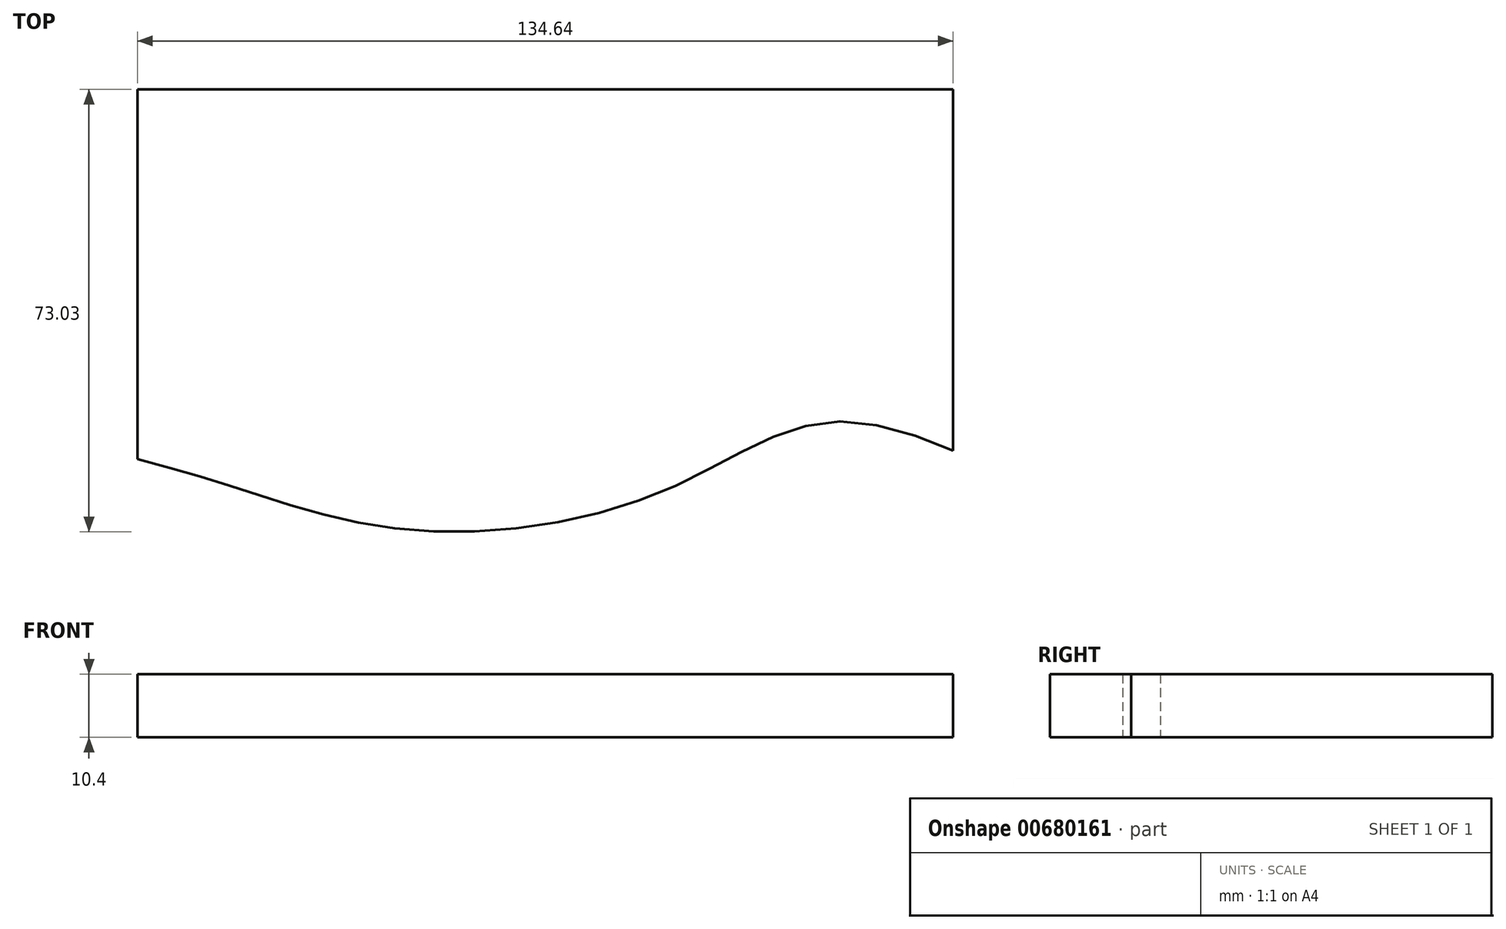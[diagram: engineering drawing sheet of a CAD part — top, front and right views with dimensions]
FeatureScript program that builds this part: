
annotation { "Feature Type Name" : "Feature", "Feature Type Description" : "" }
export const myFeature = defineFeature(function(context is Context, id is Id, definition is map)
    precondition{}
    {
        {
            var Q0;
            Q0=qCreatedBy(makeId("Top.planeOp"),FACE);
            var sketch = newSketch(context, id + "F0", { "sketchPlane" : qUnion([Q0])});
            skLineSegment(sketch, "E0.bottom", {"start": v(-68.17, 42.12) * mm, "end": v(66.47, 42.12) * mm});
            skLineSegment(sketch, "E0.left", {"start": v(-68.17, 42.12) * mm, "end": v(-68.17, -18.91) * mm});
            skLineSegment(sketch, "E0.right", {"start": v(66.47, 42.12) * mm, "end": v(66.47, -17.51) * mm});
            skFitSpline(sketch, "E1", {"points": [v(-81.38, -15.78) * mm, v(-51.87, -23.65) * mm, v(-22.35, -30.68) * mm, v(19.24, -23.93) * mm, v(48.76, -12.69) * mm, v(81.64, -25.06) * mm], "startDerivative": vector(204.36, -45.16) * mm, "endDerivative": vector(111.34, -55.88) * mm});
            skSolve(sketch);
        }
        {
            var Q0;
            Q0 = qSketchRegion(id + "F0", true);
            extrude(context, id + "F1", {"entities" : qUnion([Q0]), "depth" : 10.4 * mm, "offsetDistance" : 25 * mm});
        }
    });
